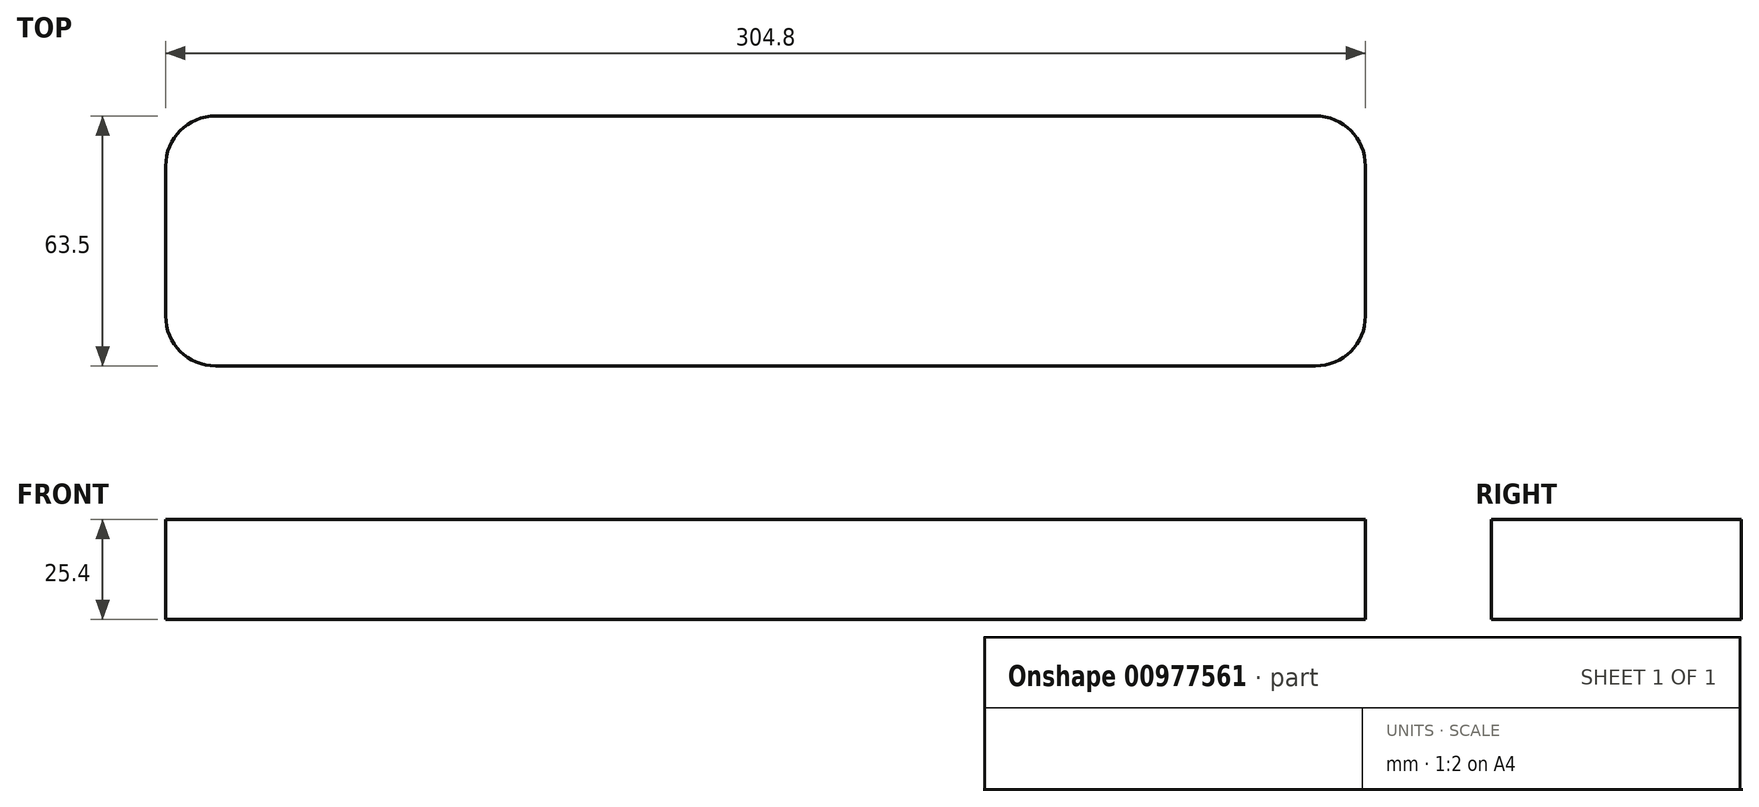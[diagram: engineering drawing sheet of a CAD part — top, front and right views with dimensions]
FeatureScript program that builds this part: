
annotation { "Feature Type Name" : "Feature", "Feature Type Description" : "" }
export const myFeature = defineFeature(function(context is Context, id is Id, definition is map)
    precondition{}
    {
        {
            var Q0;
            Q0=qCreatedBy(makeId("Top.planeOp"),FACE);
            var sketch = newSketch(context, id + "F0", { "sketchPlane" : qUnion([Q0])});
            skLineSegment(sketch, "E0.bottom", {"start": v(12.7, 0) * mm, "end": v(292.1, 0) * mm});
            skLineSegment(sketch, "E0.top", {"start": v(12.7, 63.5) * mm, "end": v(292.1, 63.5) * mm});
            skLineSegment(sketch, "E0.left", {"start": v(0, 12.7) * mm, "end": v(0, 50.8) * mm});
            skLineSegment(sketch, "E0.right", {"start": v(304.8, 12.7) * mm, "end": v(304.8, 50.8) * mm});
            skPoint(sketch, "E1.visualSharp", {"position": v(0, 63.5) * mm});
            skArc(sketch, "E1.filletArc", {"start": v(12.7, 63.5) * mm, "mid": v(3.72, 59.78) * mm, "end": v(0, 50.8) * mm});
            skPoint(sketch, "E2.visualSharp", {"position": v(304.8, 63.5) * mm});
            skArc(sketch, "E2.filletArc", {"start": v(304.8, 50.8) * mm, "mid": v(301.08, 59.78) * mm, "end": v(292.1, 63.5) * mm});
            skPoint(sketch, "E3.visualSharp", {"position": v(0, 0) * mm});
            skArc(sketch, "E3.filletArc", {"start": v(0, 12.7) * mm, "mid": v(3.72, 3.72) * mm, "end": v(12.7, 0) * mm});
            skPoint(sketch, "E4.visualSharp", {"position": v(304.8, 0) * mm});
            skArc(sketch, "E4.filletArc", {"start": v(292.1, 0) * mm, "mid": v(301.08, 3.72) * mm, "end": v(304.8, 12.7) * mm});
            skSolve(sketch);
        }
        {
            var Q0;
            Q0=makeQuery(id+"F0.imprint","IMPRINT",FACE,{"disambiguationData":[TD([[makeQuery(id+"F0.imprint","IMPRINT",EDGE,{"derivedFrom":sQuery(id+"F0.wireOp",EDGE,"E0.bottom")}),1.0]])]});
            extrude(context, id + "F1", {"entities" : qUnion([Q0]), "depth" : 25.4 * mm, "offsetDistance" : 25.4 * mm});
        }
    });
